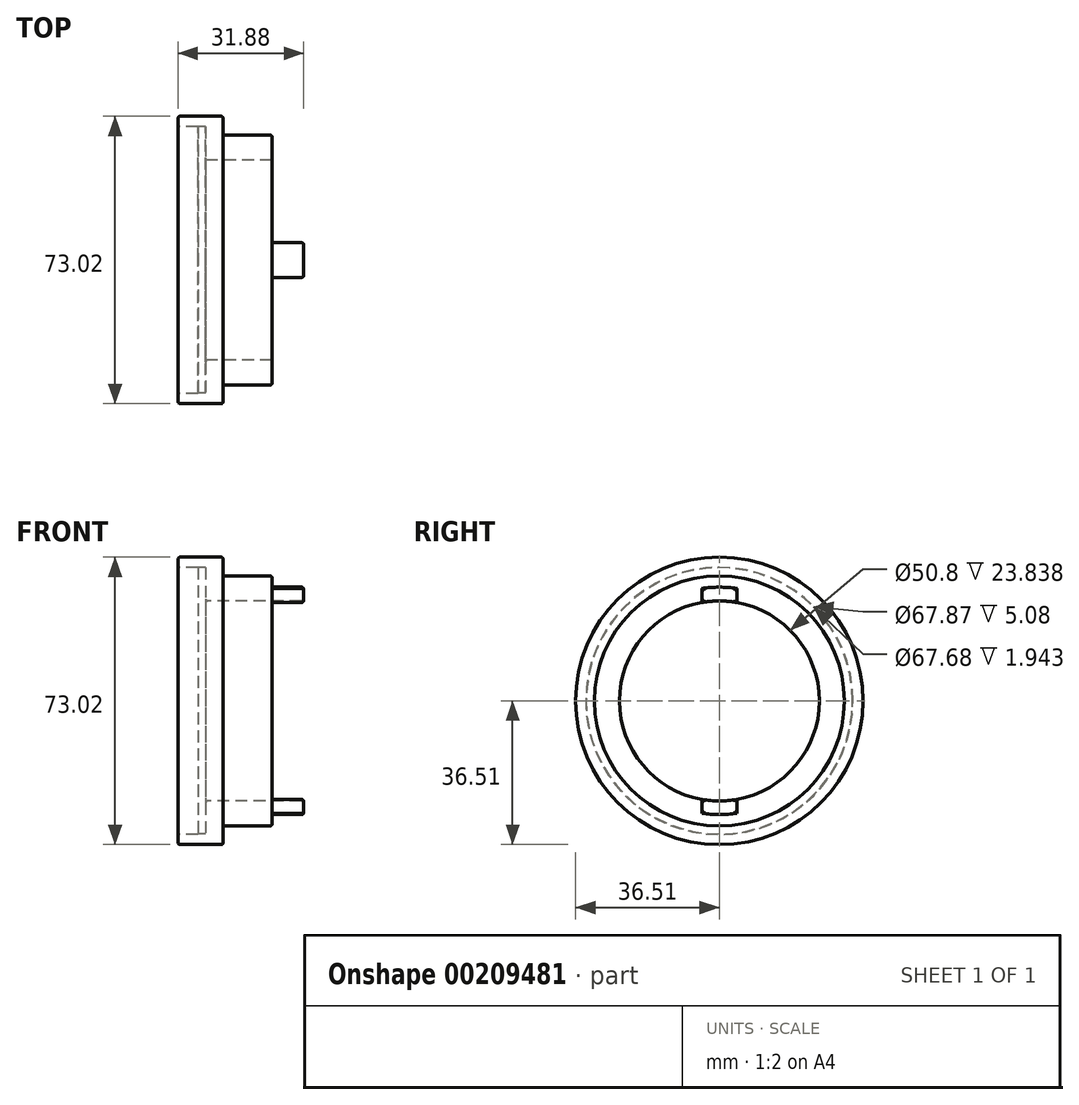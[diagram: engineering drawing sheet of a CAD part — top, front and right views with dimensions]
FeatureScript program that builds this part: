
annotation { "Feature Type Name" : "Feature", "Feature Type Description" : "" }
export const myFeature = defineFeature(function(context is Context, id is Id, definition is map)
    precondition{}
    {
        {
            var Q0;
            Q0=qCreatedBy(makeId("Front.planeOp"),FACE);
            var sketch = newSketch(context, id + "F0", { "sketchPlane" : qUnion([Q0])});
            skLineSegment(sketch, "E0", {"start": v(0, 33.93) * mm, "end": v(0, 36.51) * mm});
            skLineSegment(sketch, "E1", {"start": v(0, 36.51) * mm, "end": v(11.43, 36.51) * mm});
            skLineSegment(sketch, "E2", {"start": v(11.43, 36.51) * mm, "end": v(11.43, 33.93) * mm});
            skLineSegment(sketch, "E3", {"start": v(7.02, 29.93) * mm, "end": v(7.02, 32.79) * mm});
            skLineSegment(sketch, "E4", {"start": v(5.08, 33.93) * mm, "end": v(5.08, 33.84) * mm});
            skLineSegment(sketch, "E5", {"start": v(0, 36.51) * mm, "end": v(0, 33.93) * mm});
            skLineSegment(sketch, "E6", {"start": v(0, 33.93) * mm, "end": v(5.08, 33.93) * mm});
            skPoint(sketch, "E7.orphan", {"position": v(5.08, 29.33) * mm});
            skLineSegment(sketch, "E8", {"start": v(7.52, 0) * mm, "end": v(23.2, 0) * mm});
            skLineSegment(sketch, "E9", {"start": v(23.88, 0) * mm, "end": v(23.88, 25.4) * mm});
            skPoint(sketch, "E9.startSnap0", {"position": v(15.36, 0) * mm});
            skLineSegment(sketch, "E10", {"start": v(23.88, 25.4) * mm, "end": v(7.02, 25.4) * mm});
            skLineSegment(sketch, "E11", {"start": v(23.88, 25.4) * mm, "end": v(23.88, 31.75) * mm});
            skLineSegment(sketch, "E12", {"start": v(23.88, 31.75) * mm, "end": v(11.43, 31.75) * mm});
            skLineSegment(sketch, "E13", {"start": v(11.43, 31.75) * mm, "end": v(11.43, 33.93) * mm});
            skLineSegment(sketch, "E14", {"start": v(7.02, 25.4) * mm, "end": v(7.02, 29.93) * mm});
            skLineSegment(sketch, "E15", {"start": v(5.08, 33.84) * mm, "end": v(5.08, 33.93) * mm});
            skLineSegment(sketch, "E16", {"start": v(5.08, 33.84) * mm, "end": v(7.02, 33.84) * mm});
            skLineSegment(sketch, "E17", {"start": v(7.02, 32.79) * mm, "end": v(7.02, 33.84) * mm});
            skSolve(sketch);
        }
        {
            var Q0;
            Q0 = qSketchRegion(id + "F0", true);
            var Q1;
            Q1=sQuery(id+"F0.wireOp",EDGE,"E8");
            revolve(context, id + "F1", {"entities" : qUnion([Q0]), "axis" : qUnion([Q1]), "revolveType" : RevolveType.FULL});
        }
        {
            var Q0;
            Q0=makeQuery(id+"F1.opRevolve","SWEPT_FACE",FACE,{"disambiguationData":[OSD([sQuery(id+"F0.wireOp",EDGE,"E11")])]});
            var sketch = newSketch(context, id + "F2", { "sketchPlane" : qUnion([Q0])});
            skArc(sketch, "E18", {"start": v(-4.41, -28.55) * mm, "mid": v(0, -28.9) * mm, "end": v(4.41, -28.55) * mm});
            skArc(sketch, "E19", {"start": v(-4.41, -25.01) * mm, "mid": v(0, -25.4) * mm, "end": v(4.41, -25.01) * mm});
            skLineSegment(sketch, "E20.left", {"start": v(4.41, 28.55) * mm, "end": v(4.41, 25.01) * mm});
            skLineSegment(sketch, "E20.right", {"start": v(-4.41, 28.55) * mm, "end": v(-4.41, 25.01) * mm});
            skPoint(sketch, "E20.bottom.end.orphan", {"position": v(-4.41, 50.48) * mm});
            skPoint(sketch, "E20.bottom.start.orphan", {"position": v(4.41, 50.48) * mm});
            skLineSegment(sketch, "E21.trimOffspring", {"start": v(-4.41, -25.01) * mm, "end": v(-4.41, -28.55) * mm});
            skLineSegment(sketch, "E22.trimOffspring", {"start": v(4.41, -25.01) * mm, "end": v(4.41, -28.55) * mm});
            skArc(sketch, "E23.trimOffspring", {"start": v(4.41, 25.01) * mm, "mid": v(0, 25.4) * mm, "end": v(-4.41, 25.01) * mm});
            skArc(sketch, "E24.trimOffspring", {"start": v(4.41, 28.55) * mm, "mid": v(0, 28.9) * mm, "end": v(-4.41, 28.55) * mm});
            skPoint(sketch, "E20.top.end.orphan", {"position": v(-4.41, -50.48) * mm});
            skPoint(sketch, "E20.top.start.orphan", {"position": v(4.41, -50.48) * mm});
            skSolve(sketch);
        }
        {
            var Q0;
            Q0 = qSketchRegion(id + "F2", true);
            extrude(context, id + "F3", {"entities" : qUnion([Q0]), "operationType" : NewBodyOperationType.ADD, "depth" : 8 * mm});
        }
        {
            var Q0;
            Q0=makeQuery(id+"F3.opExtrude","CAP_EDGE",EDGE,{"disambiguationData":[OSD([sQuery(id+"F2.wireOp",EDGE,"E23.trimOffspring")])],"isStart":false});
            var Q1;
            Q1=makeQuery(id+"F3.opExtrude","CAP_EDGE",EDGE,{"disambiguationData":[OSD([sQuery(id+"F2.wireOp",EDGE,"E24.trimOffspring")])],"isStart":false});
            var Q2;
            Q2=makeQuery(id+"F3.opExtrude","CAP_EDGE",EDGE,{"disambiguationData":[OSD([sQuery(id+"F2.wireOp",EDGE,"E20.left")])],"isStart":false});
            var Q3;
            Q3=makeQuery(id+"F3.opExtrude","CAP_EDGE",EDGE,{"disambiguationData":[OSD([sQuery(id+"F2.wireOp",EDGE,"E20.right")])],"isStart":false});
            var Q4;
            Q4=makeQuery(id+"F3.opExtrude","CAP_EDGE",EDGE,{"disambiguationData":[OSD([sQuery(id+"F2.wireOp",EDGE,"E22.trimOffspring")])],"isStart":false});
            var Q5;
            Q5=makeQuery(id+"F3.opExtrude","CAP_EDGE",EDGE,{"disambiguationData":[OSD([sQuery(id+"F2.wireOp",EDGE,"E21.trimOffspring")])],"isStart":false});
            var Q6;
            Q6=makeQuery(id+"F3.opExtrude","CAP_EDGE",EDGE,{"disambiguationData":[OSD([sQuery(id+"F2.wireOp",EDGE,"E19")])],"isStart":false});
            var Q7;
            Q7=makeQuery(id+"F3.opExtrude","CAP_EDGE",EDGE,{"disambiguationData":[OSD([sQuery(id+"F2.wireOp",EDGE,"E18")])],"isStart":false});
            fillet(context, id + "F4", {"entities" : qUnion([Q0, Q1, Q2, Q3, Q4, Q5, Q6, Q7]), "radius" : 0.5 * mm, "tangentPropagation" : true, "allowEdgeOverflow" : false});
        }
        {
            var Q0;
            Q0=makeQuery(id+"F1.opRevolve","SWEPT_FACE",FACE,{"disambiguationData":[OSD([sQuery(id+"F0.wireOp",EDGE,"E12")])]});
            var Q1;
            Q1=makeQuery(id+"F1.opRevolve","SWEPT_EDGE",EDGE,{"disambiguationData":[OSD([sQuery(id+"F0.wireOp",EDGE,"E1"),sQuery(id+"F0.wireOp",EDGE,"E2")])]});
            var Q2;
            Q2=makeQuery(id+"F1.opRevolve","SWEPT_EDGE",EDGE,{"disambiguationData":[OSD([sQuery(id+"F0.wireOp",EDGE,"E1"),sQuery(id+"F0.wireOp",EDGE,"E5")])]});
            var Q3;
            Q3=makeQuery(id+"F1.opRevolve","SWEPT_EDGE",EDGE,{"disambiguationData":[OSD([sQuery(id+"F0.wireOp",EDGE,"E10"),sQuery(id+"F0.wireOp",EDGE,"E14")])]});
            fillet(context, id + "F5", {"entities" : qUnion([Q0, Q1, Q2, Q3]), "radius" : 0.5 * mm, "tangentPropagation" : true, "allowEdgeOverflow" : false});
        }
    });
